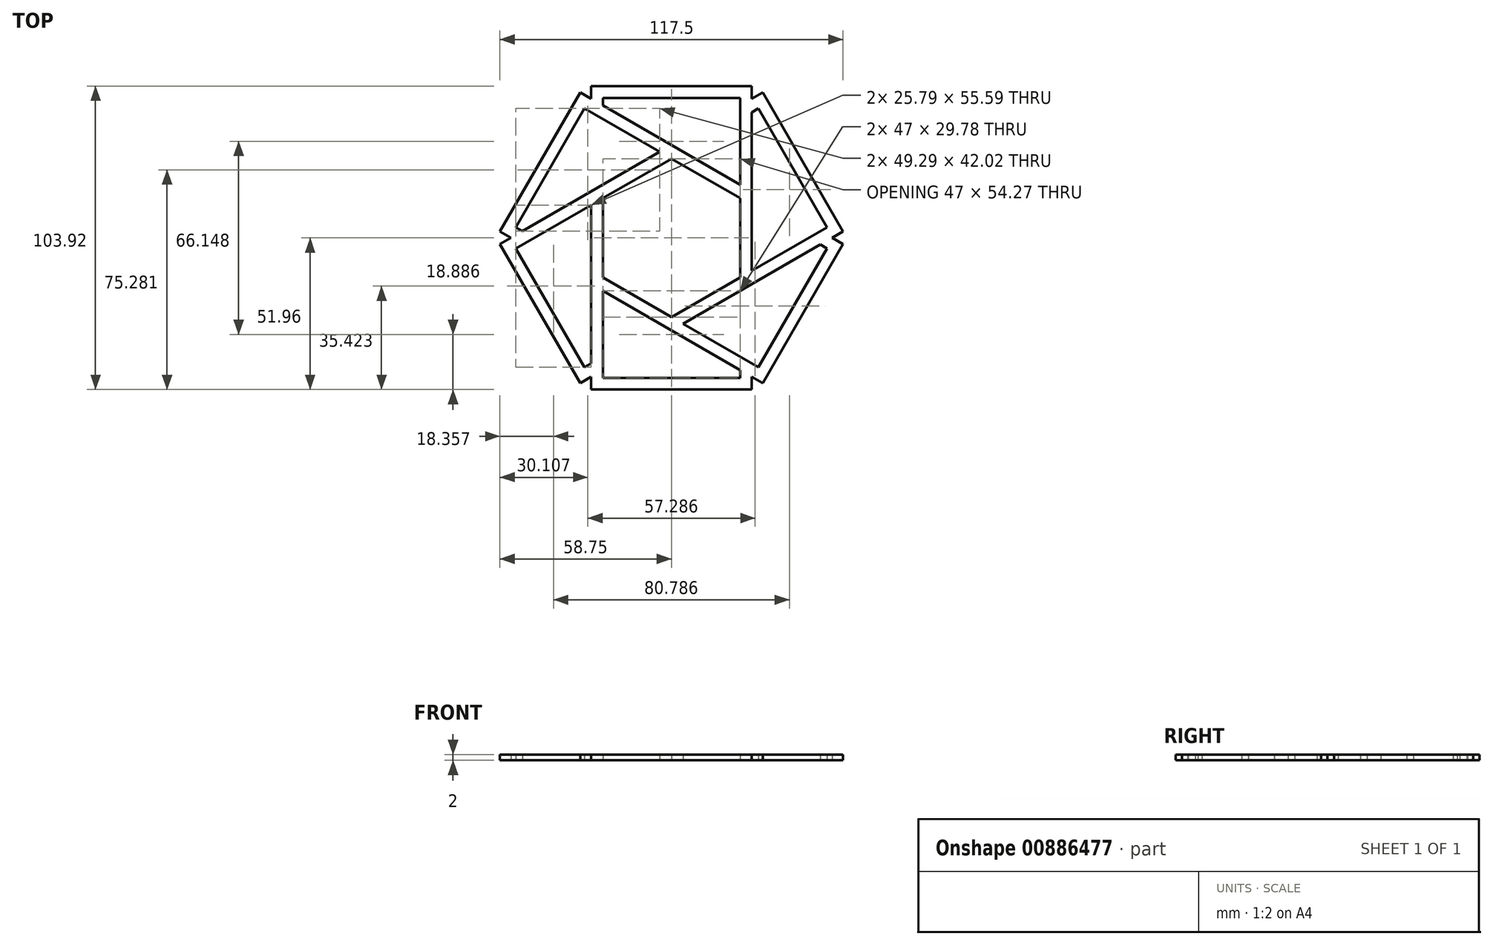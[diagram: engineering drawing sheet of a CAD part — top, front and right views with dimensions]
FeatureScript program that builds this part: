
annotation { "Feature Type Name" : "Feature", "Feature Type Description" : "" }
export const myFeature = defineFeature(function(context is Context, id is Id, definition is map)
    precondition{}
    {
        {
            var Q0;
            Q0=qCreatedBy(makeId("Top.planeOp"),FACE);
            var sketch = newSketch(context, id + "F0", { "sketchPlane" : qUnion([Q0])});
            skCircle(sketch, "E0.cCircle", {"center": v(0, 0) * mm, "radius": 60 * mm, "construction": true});
            skLineSegment(sketch, "E0.0", {"start": v(-60, 0) * mm, "end": v(-30, 51.96) * mm, "construction": true});
            skLineSegment(sketch, "E0.1", {"start": v(-30, 51.96) * mm, "end": v(30, 51.96) * mm, "construction": true});
            skLineSegment(sketch, "E0.2", {"start": v(30, 51.96) * mm, "end": v(60, 0) * mm, "construction": true});
            skLineSegment(sketch, "E0.3", {"start": v(60, 0) * mm, "end": v(30, -51.96) * mm, "construction": true});
            skLineSegment(sketch, "E0.4", {"start": v(30, -51.96) * mm, "end": v(-30, -51.96) * mm, "construction": true});
            skLineSegment(sketch, "E0.5", {"start": v(-30, -51.96) * mm, "end": v(-60, 0) * mm, "construction": true});
            skLineSegment(sketch, "E1.bottom", {"start": v(-27.5, 51.96) * mm, "end": v(27.5, 51.96) * mm});
            skLineSegment(sketch, "E1.top", {"start": v(-27.5, -51.96) * mm, "end": v(27.5, -51.96) * mm});
            skLineSegment(sketch, "E1.left", {"start": v(-27.5, 51.96) * mm, "end": v(-27.5, -51.96) * mm});
            skLineSegment(sketch, "E1.right", {"start": v(27.5, 51.96) * mm, "end": v(27.5, -51.96) * mm});
            skLineSegment(sketch, "E2.0", {"start": v(-23.5, -47.96) * mm, "end": v(23.5, -47.96) * mm});
            skLineSegment(sketch, "E2.1", {"start": v(-23.5, 47.96) * mm, "end": v(-23.5, -47.96) * mm});
            skLineSegment(sketch, "E2.2", {"start": v(-23.5, 47.96) * mm, "end": v(23.5, 47.96) * mm});
            skLineSegment(sketch, "E2.3", {"start": v(23.5, 47.96) * mm, "end": v(23.5, -47.96) * mm});
            skLineSegment(sketch, "E3.1.0", {"start": v(-29.79, -44.33) * mm, "end": v(53.29, 3.63) * mm});
            skLineSegment(sketch, "E3.1.1", {"start": v(58.75, 2.17) * mm, "end": v(31.25, 49.8) * mm});
            skLineSegment(sketch, "E3.1.2", {"start": v(-31.25, -49.8) * mm, "end": v(-58.75, -2.17) * mm});
            skLineSegment(sketch, "E3.1.3", {"start": v(-29.79, -44.33) * mm, "end": v(-53.29, -3.63) * mm});
            skLineSegment(sketch, "E3.1.4", {"start": v(-53.29, -3.63) * mm, "end": v(29.79, 44.33) * mm});
            skLineSegment(sketch, "E3.1.5", {"start": v(-58.75, -2.17) * mm, "end": v(31.25, 49.8) * mm});
            skLineSegment(sketch, "E3.1.7", {"start": v(53.29, 3.63) * mm, "end": v(29.79, 44.33) * mm});
            skLineSegment(sketch, "E3.1.8", {"start": v(-31.25, -49.8) * mm, "end": v(58.75, 2.17) * mm});
            skLineSegment(sketch, "E3.2.0", {"start": v(53.29, -3.63) * mm, "end": v(-29.79, 44.33) * mm});
            skLineSegment(sketch, "E3.2.1", {"start": v(-31.25, 49.8) * mm, "end": v(-58.75, 2.17) * mm});
            skLineSegment(sketch, "E3.2.2", {"start": v(58.75, -2.17) * mm, "end": v(31.25, -49.8) * mm});
            skLineSegment(sketch, "E3.2.3", {"start": v(53.29, -3.63) * mm, "end": v(29.79, -44.33) * mm});
            skLineSegment(sketch, "E3.2.4", {"start": v(29.79, -44.33) * mm, "end": v(-53.29, 3.63) * mm});
            skLineSegment(sketch, "E3.2.5", {"start": v(31.25, -49.8) * mm, "end": v(-58.75, 2.17) * mm});
            skLineSegment(sketch, "E3.2.7", {"start": v(-29.79, 44.33) * mm, "end": v(-53.29, 3.63) * mm});
            skLineSegment(sketch, "E3.2.8", {"start": v(58.75, -2.17) * mm, "end": v(-31.25, 49.8) * mm});
            skSolve(sketch);
        }
        {
            var Q0;
            {var subQ0=sQuery(id+"F0.wireOp",EDGE,"E3.1.4");var subQ1=sQuery(id+"F0.wireOp",EDGE,"E1.left");var subQ2=makeQuery(id+"F0.imprint","INTERSECT",VERTEX,{"derivedFrom":[subQ1,subQ0]});Q0=makeQuery(id+"F0.imprint","IMPRINT",FACE,{"disambiguationData":[TD([[makeQuery(id+"F0.imprint","IMPRINT",EDGE,{"disambiguationData":[TD([[subQ2,-1.0]])],"derivedFrom":subQ1}),1.0]])]});}
            var Q1;
            {var subQ0=sQuery(id+"F0.wireOp",EDGE,"E3.2.4");var subQ1=sQuery(id+"F0.wireOp",EDGE,"E1.left");var subQ2=makeQuery(id+"F0.imprint","INTERSECT",VERTEX,{"derivedFrom":[subQ1,subQ0]});Q1=makeQuery(id+"F0.imprint","IMPRINT",FACE,{"disambiguationData":[TD([[makeQuery(id+"F0.imprint","IMPRINT",EDGE,{"disambiguationData":[TD([[subQ2,-1.0]])],"derivedFrom":subQ1}),1.0]])]});}
            var Q2;
            {var subQ0=sQuery(id+"F0.wireOp",EDGE,"E3.2.4");var subQ1=sQuery(id+"F0.wireOp",EDGE,"E2.1");var subQ2=makeQuery(id+"F0.imprint","INTERSECT",VERTEX,{"derivedFrom":[subQ1,subQ0]});Q2=makeQuery(id+"F0.imprint","IMPRINT",FACE,{"disambiguationData":[TD([[makeQuery(id+"F0.imprint","IMPRINT",EDGE,{"disambiguationData":[TD([[subQ2,-1.0]])],"derivedFrom":subQ1}),1.0]])]});}
            var Q3;
            {var subQ0=sQuery(id+"F0.wireOp",EDGE,"E3.2.5");var subQ1=sQuery(id+"F0.wireOp",EDGE,"E1.left");var subQ2=makeQuery(id+"F0.imprint","INTERSECT",VERTEX,{"derivedFrom":[subQ1,subQ0]});Q3=makeQuery(id+"F0.imprint","IMPRINT",FACE,{"disambiguationData":[TD([[makeQuery(id+"F0.imprint","IMPRINT",EDGE,{"disambiguationData":[TD([[subQ2,-1.0]])],"derivedFrom":subQ1}),1.0]])]});}
            var Q4;
            {var subQ0=sQuery(id+"F0.wireOp",EDGE,"E3.1.8");var subQ1=sQuery(id+"F0.wireOp",EDGE,"E1.left");var subQ2=makeQuery(id+"F0.imprint","INTERSECT",VERTEX,{"derivedFrom":[subQ1,subQ0]});Q4=makeQuery(id+"F0.imprint","IMPRINT",FACE,{"disambiguationData":[TD([[makeQuery(id+"F0.imprint","IMPRINT",EDGE,{"disambiguationData":[TD([[subQ2,1.0]])],"derivedFrom":subQ1}),1.0]])]});}
            var Q5;
            {var subQ4=sQuery(id+"F0.wireOp",EDGE,"E3.1.2");Q5=makeQuery(id+"F0.imprint","IMPRINT",FACE,{"disambiguationData":[TD([[makeQuery(id+"F0.imprint","IMPRINT",EDGE,{"derivedFrom":subQ4}),-1.0]])]});}
            var Q6;
            {var subQ1=sQuery(id+"F0.wireOp",EDGE,"E1.top");Q6=makeQuery(id+"F0.imprint","IMPRINT",FACE,{"disambiguationData":[TD([[makeQuery(id+"F0.imprint","IMPRINT",EDGE,{"derivedFrom":subQ1}),1.0]])]});}
            var Q7;
            {var subQ0=sQuery(id+"F0.wireOp",EDGE,"E3.2.4");var subQ1=sQuery(id+"F0.wireOp",EDGE,"E2.3");var subQ2=makeQuery(id+"F0.imprint","INTERSECT",VERTEX,{"derivedFrom":[subQ1,subQ0]});Q7=makeQuery(id+"F0.imprint","IMPRINT",FACE,{"disambiguationData":[TD([[makeQuery(id+"F0.imprint","IMPRINT",EDGE,{"disambiguationData":[TD([[subQ2,-1.0]])],"derivedFrom":subQ1}),-1.0]])]});}
            var Q8;
            {var subQ0=sQuery(id+"F0.wireOp",EDGE,"E3.2.5");var subQ1=sQuery(id+"F0.wireOp",EDGE,"E1.right");var subQ2=makeQuery(id+"F0.imprint","INTERSECT",VERTEX,{"derivedFrom":[subQ1,subQ0]});Q8=makeQuery(id+"F0.imprint","IMPRINT",FACE,{"disambiguationData":[TD([[makeQuery(id+"F0.imprint","IMPRINT",EDGE,{"disambiguationData":[TD([[subQ2,1.0]])],"derivedFrom":subQ1}),-1.0]])]});}
            var Q9;
            {var subQ0=sQuery(id+"F0.wireOp",EDGE,"E3.2.5");var subQ1=sQuery(id+"F0.wireOp",EDGE,"E3.1.0");var subQ2=makeQuery(id+"F0.imprint","INTERSECT",VERTEX,{"derivedFrom":[subQ1,subQ0]});Q9=makeQuery(id+"F0.imprint","IMPRINT",FACE,{"disambiguationData":[TD([[makeQuery(id+"F0.imprint","IMPRINT",EDGE,{"disambiguationData":[TD([[subQ2,-1.0]])],"derivedFrom":subQ1}),-1.0]])]});}
            var Q10;
            {var subQ0=sQuery(id+"F0.wireOp",EDGE,"E3.1.0");var subQ1=sQuery(id+"F0.wireOp",EDGE,"E2.3");var subQ2=makeQuery(id+"F0.imprint","INTERSECT",VERTEX,{"derivedFrom":[subQ1,subQ0]});Q10=makeQuery(id+"F0.imprint","IMPRINT",FACE,{"disambiguationData":[TD([[makeQuery(id+"F0.imprint","IMPRINT",EDGE,{"disambiguationData":[TD([[subQ2,-1.0]])],"derivedFrom":subQ1}),-1.0]])]});}
            var Q11;
            {var subQ0=sQuery(id+"F0.wireOp",EDGE,"E3.1.0");var subQ1=sQuery(id+"F0.wireOp",EDGE,"E1.right");var subQ2=makeQuery(id+"F0.imprint","INTERSECT",VERTEX,{"derivedFrom":[subQ1,subQ0]});Q11=makeQuery(id+"F0.imprint","IMPRINT",FACE,{"disambiguationData":[TD([[makeQuery(id+"F0.imprint","IMPRINT",EDGE,{"disambiguationData":[TD([[subQ2,-1.0]])],"derivedFrom":subQ1}),-1.0]])]});}
            var Q12;
            {var subQ0=sQuery(id+"F0.wireOp",EDGE,"E3.2.2");Q12=makeQuery(id+"F0.imprint","IMPRINT",FACE,{"disambiguationData":[TD([[makeQuery(id+"F0.imprint","IMPRINT",EDGE,{"derivedFrom":subQ0}),-1.0]])]});}
            var Q13;
            {var subQ0=sQuery(id+"F0.wireOp",EDGE,"E3.1.0");var subQ1=sQuery(id+"F0.wireOp",EDGE,"E1.right");var subQ2=makeQuery(id+"F0.imprint","INTERSECT",VERTEX,{"derivedFrom":[subQ1,subQ0]});Q13=makeQuery(id+"F0.imprint","IMPRINT",FACE,{"disambiguationData":[TD([[makeQuery(id+"F0.imprint","IMPRINT",EDGE,{"disambiguationData":[TD([[subQ2,-1.0]])],"derivedFrom":subQ1}),1.0]])]});}
            var Q14;
            {var subQ0=sQuery(id+"F0.wireOp",EDGE,"E3.2.5");var subQ1=sQuery(id+"F0.wireOp",EDGE,"E3.1.4");var subQ2=makeQuery(id+"F0.imprint","INTERSECT",VERTEX,{"derivedFrom":[subQ1,subQ0]});Q14=makeQuery(id+"F0.imprint","IMPRINT",FACE,{"disambiguationData":[TD([[makeQuery(id+"F0.imprint","IMPRINT",EDGE,{"disambiguationData":[TD([[subQ2,-1.0]])],"derivedFrom":subQ1}),1.0]])]});}
            var Q15;
            {var subQ0=sQuery(id+"F0.wireOp",EDGE,"E3.1.5");var subQ1=sQuery(id+"F0.wireOp",EDGE,"E1.left");var subQ2=makeQuery(id+"F0.imprint","INTERSECT",VERTEX,{"derivedFrom":[subQ1,subQ0]});Q15=makeQuery(id+"F0.imprint","IMPRINT",FACE,{"disambiguationData":[TD([[makeQuery(id+"F0.imprint","IMPRINT",EDGE,{"disambiguationData":[TD([[subQ2,-1.0]])],"derivedFrom":subQ1}),-1.0]])]});}
            var Q16;
            {var subQ0=sQuery(id+"F0.wireOp",EDGE,"E3.2.1");Q16=makeQuery(id+"F0.imprint","IMPRINT",FACE,{"disambiguationData":[TD([[makeQuery(id+"F0.imprint","IMPRINT",EDGE,{"derivedFrom":subQ0}),1.0]])]});}
            var Q17;
            {var subQ0=sQuery(id+"F0.wireOp",EDGE,"E3.1.5");var subQ1=sQuery(id+"F0.wireOp",EDGE,"E2.1");var subQ2=makeQuery(id+"F0.imprint","INTERSECT",VERTEX,{"derivedFrom":[subQ1,subQ0]});Q17=makeQuery(id+"F0.imprint","IMPRINT",FACE,{"disambiguationData":[TD([[makeQuery(id+"F0.imprint","IMPRINT",EDGE,{"disambiguationData":[TD([[subQ2,-1.0]])],"derivedFrom":subQ1}),1.0]])]});}
            var Q18;
            {var subQ0=sQuery(id+"F0.wireOp",EDGE,"E3.1.5");var subQ1=sQuery(id+"F0.wireOp",EDGE,"E1.left");var subQ2=makeQuery(id+"F0.imprint","INTERSECT",VERTEX,{"derivedFrom":[subQ1,subQ0]});Q18=makeQuery(id+"F0.imprint","IMPRINT",FACE,{"disambiguationData":[TD([[makeQuery(id+"F0.imprint","IMPRINT",EDGE,{"disambiguationData":[TD([[subQ2,-1.0]])],"derivedFrom":subQ1}),1.0]])]});}
            var Q19;
            {var subQ0=sQuery(id+"F0.wireOp",EDGE,"E3.2.8");var subQ1=sQuery(id+"F0.wireOp",EDGE,"E2.1");var subQ2=makeQuery(id+"F0.imprint","INTERSECT",VERTEX,{"derivedFrom":[subQ1,subQ0]});Q19=makeQuery(id+"F0.imprint","IMPRINT",FACE,{"disambiguationData":[TD([[makeQuery(id+"F0.imprint","IMPRINT",EDGE,{"disambiguationData":[TD([[subQ2,-1.0]])],"derivedFrom":subQ1}),1.0]])]});}
            var Q20;
            {var subQ0=sQuery(id+"F0.wireOp",EDGE,"E3.2.8");var subQ1=sQuery(id+"F0.wireOp",EDGE,"E1.left");var subQ2=makeQuery(id+"F0.imprint","INTERSECT",VERTEX,{"derivedFrom":[subQ1,subQ0]});Q20=makeQuery(id+"F0.imprint","IMPRINT",FACE,{"disambiguationData":[TD([[makeQuery(id+"F0.imprint","IMPRINT",EDGE,{"disambiguationData":[TD([[subQ2,-1.0]])],"derivedFrom":subQ1}),1.0]])]});}
            var Q21;
            {var subQ5=sQuery(id+"F0.wireOp",EDGE,"E1.bottom");Q21=makeQuery(id+"F0.imprint","IMPRINT",FACE,{"disambiguationData":[TD([[makeQuery(id+"F0.imprint","IMPRINT",EDGE,{"derivedFrom":subQ5}),-1.0]])]});}
            var Q22;
            {var subQ0=sQuery(id+"F0.wireOp",EDGE,"E3.2.0");var subQ1=sQuery(id+"F0.wireOp",EDGE,"E3.1.4");var subQ2=makeQuery(id+"F0.imprint","INTERSECT",VERTEX,{"derivedFrom":[subQ1,subQ0]});Q22=makeQuery(id+"F0.imprint","IMPRINT",FACE,{"disambiguationData":[TD([[makeQuery(id+"F0.imprint","IMPRINT",EDGE,{"disambiguationData":[TD([[subQ2,-1.0]])],"derivedFrom":subQ1}),1.0]])]});}
            var Q23;
            {var subQ0=sQuery(id+"F0.wireOp",EDGE,"E3.2.8");var subQ1=sQuery(id+"F0.wireOp",EDGE,"E2.3");var subQ2=makeQuery(id+"F0.imprint","INTERSECT",VERTEX,{"derivedFrom":[subQ1,subQ0]});Q23=makeQuery(id+"F0.imprint","IMPRINT",FACE,{"disambiguationData":[TD([[makeQuery(id+"F0.imprint","IMPRINT",EDGE,{"disambiguationData":[TD([[subQ2,-1.0]])],"derivedFrom":subQ1}),-1.0]])]});}
            var Q24;
            {var subQ0=sQuery(id+"F0.wireOp",EDGE,"E3.1.4");var subQ1=sQuery(id+"F0.wireOp",EDGE,"E1.right");var subQ2=makeQuery(id+"F0.imprint","INTERSECT",VERTEX,{"derivedFrom":[subQ1,subQ0]});Q24=makeQuery(id+"F0.imprint","IMPRINT",FACE,{"disambiguationData":[TD([[makeQuery(id+"F0.imprint","IMPRINT",EDGE,{"disambiguationData":[TD([[subQ2,-1.0]])],"derivedFrom":subQ1}),-1.0]])]});}
            var Q25;
            {var subQ0=sQuery(id+"F0.wireOp",EDGE,"E3.1.5");var subQ1=sQuery(id+"F0.wireOp",EDGE,"E1.right");var subQ2=makeQuery(id+"F0.imprint","INTERSECT",VERTEX,{"derivedFrom":[subQ1,subQ0]});Q25=makeQuery(id+"F0.imprint","IMPRINT",FACE,{"disambiguationData":[TD([[makeQuery(id+"F0.imprint","IMPRINT",EDGE,{"disambiguationData":[TD([[subQ2,-1.0]])],"derivedFrom":subQ1}),-1.0]])]});}
            var Q26;
            {var subQ4=sQuery(id+"F0.wireOp",EDGE,"E3.1.1");Q26=makeQuery(id+"F0.imprint","IMPRINT",FACE,{"disambiguationData":[TD([[makeQuery(id+"F0.imprint","IMPRINT",EDGE,{"derivedFrom":subQ4}),1.0]])]});}
            var Q27;
            {var subQ0=sQuery(id+"F0.wireOp",EDGE,"E3.2.8");var subQ1=sQuery(id+"F0.wireOp",EDGE,"E1.right");var subQ2=makeQuery(id+"F0.imprint","INTERSECT",VERTEX,{"derivedFrom":[subQ1,subQ0]});Q27=makeQuery(id+"F0.imprint","IMPRINT",FACE,{"disambiguationData":[TD([[makeQuery(id+"F0.imprint","IMPRINT",EDGE,{"disambiguationData":[TD([[subQ2,-1.0]])],"derivedFrom":subQ1}),-1.0]])]});}
            var Q28;
            {var subQ0=sQuery(id+"F0.wireOp",EDGE,"E3.2.0");var subQ1=sQuery(id+"F0.wireOp",EDGE,"E1.right");var subQ2=makeQuery(id+"F0.imprint","INTERSECT",VERTEX,{"derivedFrom":[subQ1,subQ0]});Q28=makeQuery(id+"F0.imprint","IMPRINT",FACE,{"disambiguationData":[TD([[makeQuery(id+"F0.imprint","IMPRINT",EDGE,{"disambiguationData":[TD([[subQ2,-1.0]])],"derivedFrom":subQ1}),-1.0]])]});}
            var Q29;
            {var subQ0=sQuery(id+"F0.wireOp",EDGE,"E3.2.0");var subQ1=sQuery(id+"F0.wireOp",EDGE,"E3.1.0");var subQ2=makeQuery(id+"F0.imprint","INTERSECT",VERTEX,{"derivedFrom":[subQ1,subQ0]});Q29=makeQuery(id+"F0.imprint","IMPRINT",FACE,{"disambiguationData":[TD([[makeQuery(id+"F0.imprint","IMPRINT",EDGE,{"disambiguationData":[TD([[subQ2,-1.0]])],"derivedFrom":subQ1}),-1.0]])]});}
            extrude(context, id + "F1", {"entities" : qUnion([Q0, Q1, Q2, Q3, Q4, Q5, Q6, Q7, Q8, Q9, Q10, Q11, Q12, Q13, Q14, Q15, Q16, Q17, Q18, Q19, Q20, Q21, Q22, Q23, Q24, Q25, Q26, Q27, Q28, Q29]), "depth" : 2 * mm, "offsetDistance" : 25 * mm});
        }
    });
